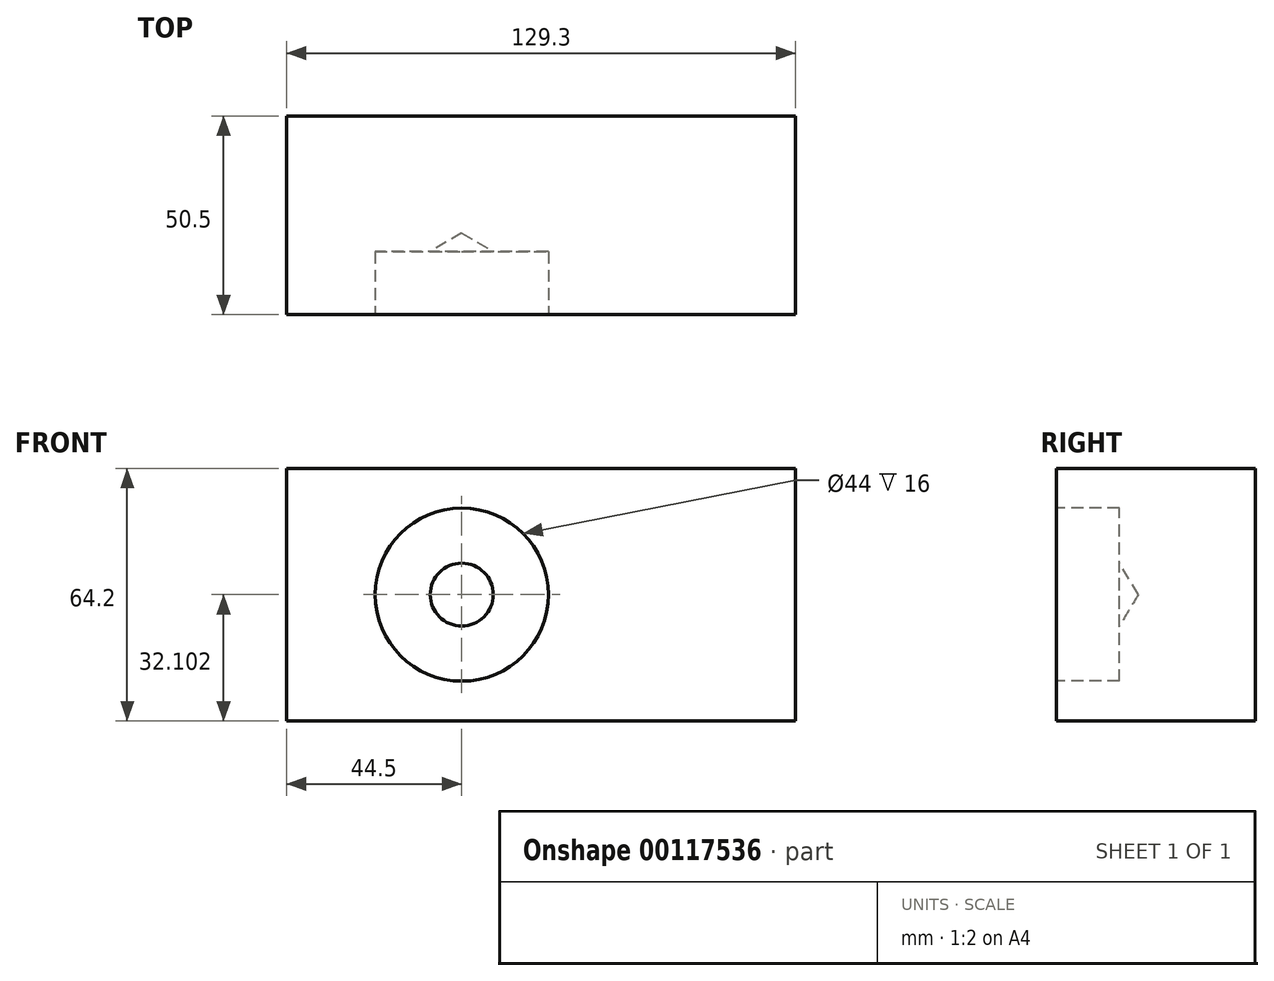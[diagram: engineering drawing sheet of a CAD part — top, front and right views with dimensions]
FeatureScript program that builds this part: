
annotation { "Feature Type Name" : "Feature", "Feature Type Description" : "" }
export const myFeature = defineFeature(function(context is Context, id is Id, definition is map)
    precondition{}
    {
        {
            var Q0;
            Q0=qCreatedBy(makeId("Front.planeOp"),FACE);
            var sketch = newSketch(context, id + "F0", { "sketchPlane" : qUnion([Q0])});
            skLineSegment(sketch, "E0.bottom", {"start": v(-96.53, 53.44) * mm, "end": v(32.77, 53.44) * mm});
            skLineSegment(sketch, "E0.top", {"start": v(-96.53, -10.76) * mm, "end": v(32.77, -10.76) * mm});
            skLineSegment(sketch, "E0.left", {"start": v(-96.53, 53.44) * mm, "end": v(-96.53, -10.76) * mm});
            skLineSegment(sketch, "E0.right", {"start": v(32.77, 53.44) * mm, "end": v(32.77, -10.76) * mm});
            skSolve(sketch);
        }
        {
            var Q0;
            Q0 = qSketchRegion(id + "F0", true);
            extrude(context, id + "F1", {"entities" : qUnion([Q0]), "depth" : 50.5 * mm});
        }
        {
            var Q0;
            Q0=makeQuery(id+"F1.opExtrude","CAP_FACE",FACE,{"disambiguationData":[OSD([sQuery(id+"F0.wireOp",EDGE,"E0.bottom"),sQuery(id+"F0.wireOp",EDGE,"E0.top"),sQuery(id+"F0.wireOp",EDGE,"E0.left"),sQuery(id+"F0.wireOp",EDGE,"E0.right")])],"isStart":false});
            var sketch = newSketch(context, id + "F2", { "sketchPlane" : qUnion([Q0])});
            skLineSegment(sketch, "E1", {"start": v(32.77, 21.34) * mm, "end": v(-11.73, 21.34) * mm});
            skCircle(sketch, "E2", {"center": v(-11.73, 21.34) * mm, "radius": 8 * mm});
            skCircle(sketch, "E3", {"center": v(-11.73, 21.34) * mm, "radius": 22 * mm});
            skLineSegment(sketch, "E4", {"start": v(-96.53, 21.34) * mm, "end": v(-52.03, 21.34) * mm});
            skCircle(sketch, "E5", {"center": v(-52.03, 21.34) * mm, "radius": 11.5 * mm});
            skCircle(sketch, "E6", {"center": v(-52.03, 21.34) * mm, "radius": 8.05 * mm});
            skCircle(sketch, "E7", {"center": v(-52.03, 21.34) * mm, "radius": 22 * mm});
            skSolve(sketch);
        }
        {
            var Q0;
            Q0=sQuery(id+"F2.wireOp",VERTEX,"E4.end");
            var Q1;
            Q1=makeQuery(id+"F1.opExtrude","SWEPT_BODY",BODY,{"disambiguationData":[OSD([sQuery(id+"F0.wireOp",EDGE,"E0.bottom"),sQuery(id+"F0.wireOp",EDGE,"E0.top"),sQuery(id+"F0.wireOp",EDGE,"E0.left"),sQuery(id+"F0.wireOp",EDGE,"E0.right")])]});
            hole(context, id + "F3", {"style" : HoleStyle.C_BORE, "endStyle" : HoleEndStyle.BLIND, "holeDiameter" : 16 * mm, "cBoreDiameter" : 44 * mm, "cBoreDepth" : 16 * mm, "holeDepth" : 16 * mm, "locations" : qUnion([Q0]), "scope" : qUnion([Q1])});
        }
    });
